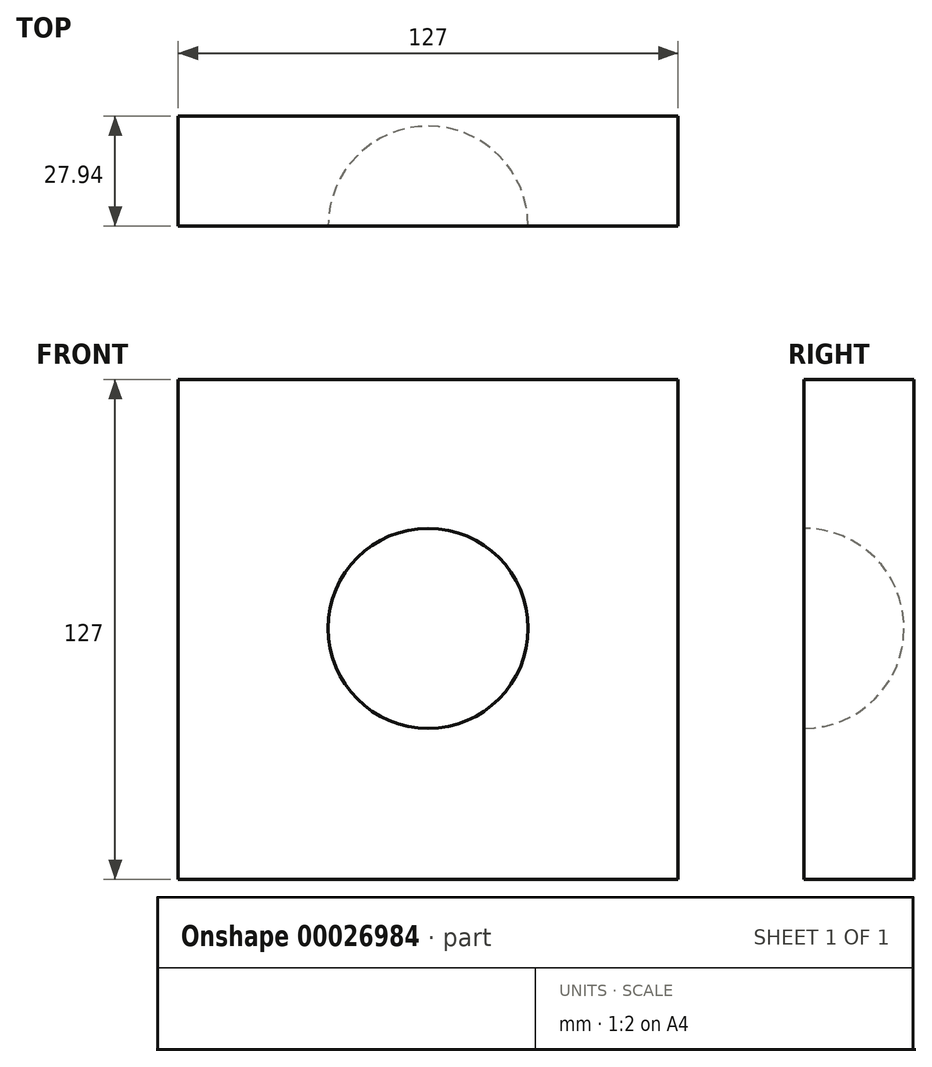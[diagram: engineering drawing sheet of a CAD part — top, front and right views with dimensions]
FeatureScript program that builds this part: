
annotation { "Feature Type Name" : "Feature", "Feature Type Description" : "" }
export const myFeature = defineFeature(function(context is Context, id is Id, definition is map)
    precondition{}
    {
        {
            var Q0;
            Q0=qCreatedBy(makeId("Front.planeOp"),FACE);
            var sketch = newSketch(context, id + "F0", { "sketchPlane" : qUnion([Q0])});
            skLineSegment(sketch, "E0.bottom", {"start": v(-34.18, 73.98) * mm, "end": v(92.82, 73.98) * mm});
            skLineSegment(sketch, "E0.top", {"start": v(-34.18, -53.02) * mm, "end": v(92.82, -53.02) * mm});
            skLineSegment(sketch, "E0.left", {"start": v(-34.18, 73.98) * mm, "end": v(-34.18, -53.02) * mm});
            skLineSegment(sketch, "E0.right", {"start": v(92.82, 73.98) * mm, "end": v(92.82, -53.02) * mm});
            skSolve(sketch);
        }
        {
            var Q0;
            Q0=makeQuery(id+"F0.imprint","IMPRINT",FACE,{"disambiguationData":[TD([[makeQuery(id+"F0.imprint","IMPRINT",EDGE,{"derivedFrom":sQuery(id+"F0.wireOp",EDGE,"E0.bottom")}),-1.0]])]});
            extrude(context, id + "F1", {"entities" : qUnion([Q0]), "depth" : 27.94 * mm});
        }
        {
            var Q0;
            Q0=makeQuery(id+"F1.opExtrude","CAP_FACE",FACE,{"disambiguationData":[OSD([sQuery(id+"F0.wireOp",EDGE,"E0.bottom"),sQuery(id+"F0.wireOp",EDGE,"E0.top"),sQuery(id+"F0.wireOp",EDGE,"E0.left"),sQuery(id+"F0.wireOp",EDGE,"E0.right")])],"isStart":false});
            var sketch = newSketch(context, id + "F2", { "sketchPlane" : qUnion([Q0])});
            skPoint(sketch, "E1", {"position": v(29.32, 73.98) * mm});
            skPoint(sketch, "E2", {"position": v(29.32, -53.02) * mm});
            skPoint(sketch, "E3", {"position": v(29.32, 36.18) * mm});
            skPoint(sketch, "E4", {"position": v(29.32, -14.62) * mm});
            skPoint(sketch, "E5", {"position": v(54.72, 10.78) * mm});
            skLineSegment(sketch, "E6", {"start": v(29.32, 36.18) * mm, "end": v(29.32, -14.62) * mm});
            skPoint(sketch, "E7", {"position": v(29.32, 10.78) * mm});
            skArc(sketch, "E8", {"start": v(29.32, -14.62) * mm, "mid": v(54.72, 10.78) * mm, "end": v(29.32, 36.18) * mm});
            skSolve(sketch);
        }
        {
            var Q0;
            Q0=makeQuery(id+"F2.imprint","IMPRINT",FACE,{"disambiguationData":[TD([[makeQuery(id+"F2.imprint","IMPRINT",EDGE,{"derivedFrom":sQuery(id+"F2.wireOp",EDGE,"E6")}),1.0]])]});
            var Q1;
            Q1=sQuery(id+"F2.wireOp",EDGE,"E6");
            revolve(context, id + "F3", {"operationType" : NewBodyOperationType.REMOVE, "entities" : qUnion([Q0]), "axis" : qUnion([Q1]), "revolveType" : RevolveType.FULL, "oppositeDirection" : true});
        }
    });
